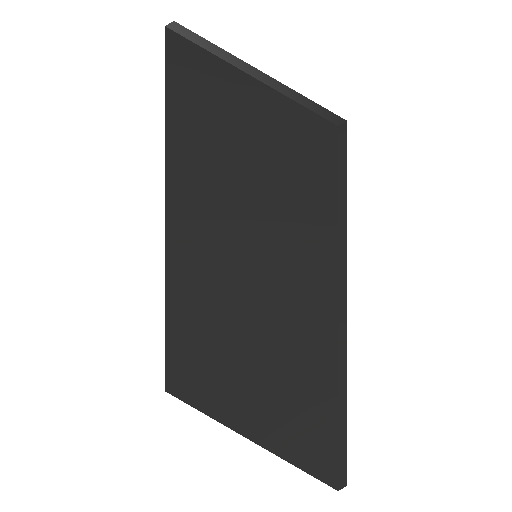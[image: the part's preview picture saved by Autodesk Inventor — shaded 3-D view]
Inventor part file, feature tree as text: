
AUTODESK INVENTOR PART (.ipt)
format: ipt  version: 2025 (Build 290162000, 162)  size: 80,896 bytes
history: native  units: in
note: dims shown in document units (in); Inventor stores cm internally (conversion verified against a paired STEP export)
features: extrude x1, sketch x1
ambient origin geometry x8: Origin, YZ Plane, XZ Plane, XY Plane, X Axis, Y Axis, Z Axis, Center Point
bodies: Solid1 (feature_tree)
feature tree (2):
  extrude  "Extrusion1"  Depth=1.6535in
  sketch  "Sketch1"  dims[d0=0.9055in d1=1.6535in d2=0.0472in d3=0.0in]
